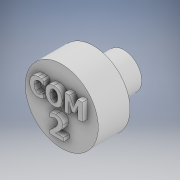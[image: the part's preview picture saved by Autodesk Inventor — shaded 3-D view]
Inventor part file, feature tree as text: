
AUTODESK INVENTOR PART (.ipt)
format: ipt  version: 2022 (Build 260153000, 153)  size: 223,744 bytes
history: native  units: in
note: dims shown in document units (in); Inventor stores cm internally (conversion verified against a paired STEP export)
features: sketch x3, extrude x3
ambient origin geometry x8: Origin, YZ Plane, XZ Plane, XY Plane, X Axis, Y Axis, Z Axis, Center Point
bodies: Solid1 (feature_tree)
feature tree (6):
  sketch  "Sketch1"  dims[d0=0.4898in d1=0.0185in]
  extrude  "Extrusion1"  Depth=0.0185in
  extrude  "Extrusion2"  Depth=0.1969in TaperAngle=0.0deg
  sketch  "Sketch2"  dims[d2=0.1969in d3=0.0in d4=0.189in d5=0.0in]
  extrude  "Extrusion3"  [1 undecoded]
  sketch  "Sketch3"  dims[d6=0.0354in d7=0.0in]
note: 1 required parameter value undecoded (feature->parameter linkage not recoverable at this tier; creation-order binding heuristic only, values carry confidence <= 0.55)
